# Revit family: Storage-Teknion-CQCPT_Routes_Personal_Tote-R2018
name_source: partatom
category: Furniture
revit_build: Autodesk Revit 2018 (Build: 20190510_1515(x64)
units: mm (PartAtom-declared; Revit-internal decimal feet)

## family parameters
Always vertical = Yes
Cut with Voids When Loaded = No
OmniClass Number = 23.40.20.00
OmniClass Title = General Furniture and Specialties
Room Calculation Point = No
Shared = Yes
Work Plane-Based = No

## types (2) — shared parameters
Assembly Code = E2020200
Manufacturer = Teknion
Manufacturer Fax = 416.661.4586
Part Number = CQCPT
Product Documentation Link = https://assets.teknion.com
Product Line = Routes
Product Page URL = https://www.teknion.com
Series = Routes
Sustainability Data = https://www.teknion.com
URL = www.teknion.com
Unit Weight URL = http://www.teknion.com
Warranty = http://www.teknion.com

## per-type parameters (varying)
| type | 2D Lock | Description | Model |
| Drawer Lock, Keyed Random, 14"d x 22"w | Yes | Routes Personal Tote, Drawer Lock, Keyed Random, 14" Depth, 22" Width | CQCPTY1422 |
| No Drawer Lock, 14"d x 22"w | No | Routes Personal Tote, No Drawer Lock, 14" Depth, 22" Width | CQCPTN1422 |

## geometry (parser evidence)
native form markers: Blend x2, Sweep x2
no freeform markers — native parametric forms only
